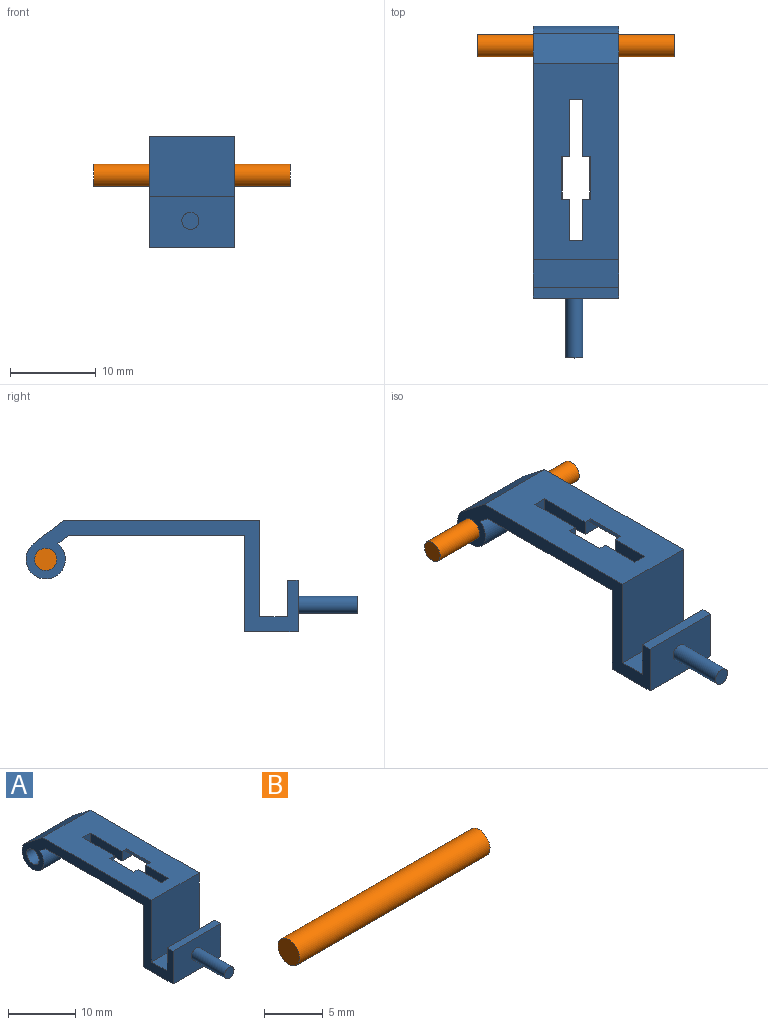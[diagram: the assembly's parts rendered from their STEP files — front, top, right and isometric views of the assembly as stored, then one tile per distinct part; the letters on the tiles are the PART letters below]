
ASSEMBLY  parts=2 mates=1
PART A: 31 faces, bbox 10x38.8x13 mm
  f0: plane 20.57x10mm, normal (0,0,-1), area 157.2mm2, adj f2,f3,f13,f14,f17,f18,f19,f20
  f1: plane 22.92x10mm, normal (0,0,1), area 193.2mm2, adj f5,f6,f13,f14,f17,f18,f19,f20
  f2: plane 11.25x10mm, normal (0,1,0), area 112.5mm2, adj f0,f12,f13,f14
  f3: plane 10x1.26mm, normal (0,-0.62,-0.79), area 16mm2, adj f0,f4,f13,f14
  f4: cylinder r=2.3mm len=10mm, axis (-1,0,0), area 113.9mm2, adj f3,f5,f13,f14
  f5: plane 10x3.49mm, normal (0,0.62,0.79), area 44.4mm2, adj f1,f4,f13,f14
  f6: plane 11.25x10mm, normal (0,-1,0), area 112.5mm2, adj f1,f7,f13,f14
  f7: plane 10x3.26mm, normal (0,0,1), area 32.6mm2, adj f6,f8,f13,f14
  f8: plane 10x4.25mm, normal (0,1,0), area 42.5mm2, adj f7,f9,f13,f14
  f9: plane 10x1.25mm, normal (0,0,1), area 12.5mm2, adj f8,f10,f13,f14
  f10: plane 10x6mm, normal (0,-1,0), area 56.9mm2, adj f9,f12,f13,f14,f15
  f11: cylinder r=1.3mm len=10mm, axis (-1,0,0), area 81.7mm2, adj f13,f14
  f12: plane 10x6.26mm, normal (0,0,-1), area 62.6mm2, adj f2,f10,f13,f14
  f13: plane 31.81x13mm, normal (1,0,0), area 88.1mm2, adj f0,f1,f2,f3,f4,f5,f6,f7
  f14: plane 31.81x13mm, normal (-1,0,0), area 88.1mm2, adj f0,f1,f2,f3,f4,f5,f6,f7
  f15: cylinder r=1mm len=7mm, axis (0,1,0), area 44mm2, adj f10,f16
  f16: plane 2x2mm, normal (0,-1,0), area 3.1mm2, adj f15
  f17: plane 6.68x1.75mm, normal (1,0,0), area 11.7mm2, adj f0,f1,f18,f26
  f18: plane 2.2x1.75mm, normal (0,-1,0), area 2.4mm2, adj f0,f1,f17,f27,f29
  f19: plane 2.2x1.75mm, normal (0,1,0), area 2.4mm2, adj f0,f1,f20,f27,f29
  f20: plane 4.85x1.75mm, normal (1,0,0), area 8.5mm2, adj f0,f1,f19,f21
  f21: plane 1.75x1.61mm, normal (0,1,0), area 2.8mm2, adj f0,f1,f20,f22
  f22: plane 4.85x1.75mm, normal (-1,0,0), area 8.5mm2, adj f0,f1,f21,f23
  f23: plane 2.2x1.75mm, normal (0,1,0), area 2.4mm2, adj f0,f1,f22,f28,f30
  f24: plane 2.2x1.75mm, normal (0,-1,0), area 2.4mm2, adj f0,f1,f25,f28,f30
  f25: plane 6.68x1.75mm, normal (-1,0,0), area 11.7mm2, adj f0,f1,f24,f26
  f26: plane 1.75x1.61mm, normal (0,-1,0), area 2.8mm2, adj f0,f1,f17,f25
  f27: plane 5x1.4mm, normal (0.71,0,-0.71), area 9.9mm2, adj f0,f18,f19,f29
  f28: plane 5x1.4mm, normal (-0.71,0,-0.71), area 9.9mm2, adj f0,f23,f24,f30
  f29: plane 5x0.35mm, normal (0.92,0,0.38), area 1.9mm2, adj f1,f18,f19,f27
  f30: plane 5x0.35mm, normal (-0.92,0,0.38), area 1.9mm2, adj f1,f23,f24,f28
PART B: 3 faces, bbox 23x2.6x2.6 mm
  f0: cylinder r=1.3mm len=23mm, axis (-1,0,0), area 187.9mm2, adj f1,f2
  f1: plane 2.6x2.6mm, normal (1,0,0), area 5.3mm2, adj f0
  f2: plane 2.6x2.6mm, normal (-1,0,0), area 5.3mm2, adj f0
PLACE A t=(0,3.08,0)mm
PLACE B t=(-6.5,32.59,-1.81)mm
MATE fastened B.f0 <-> A.f4  axis (-1,0,0) through (5,32.59,-1.81)mm
